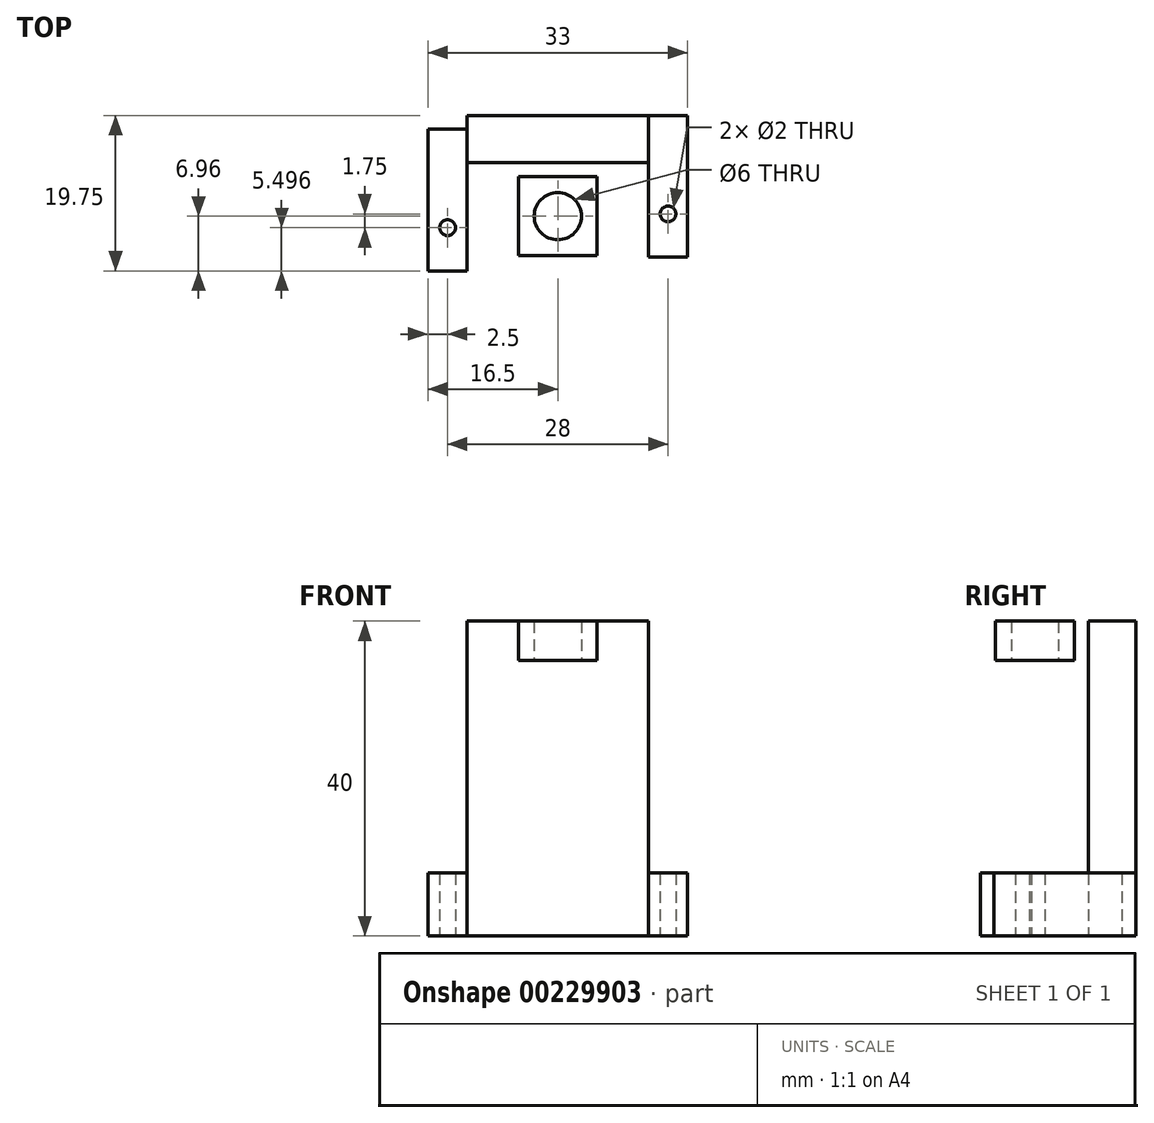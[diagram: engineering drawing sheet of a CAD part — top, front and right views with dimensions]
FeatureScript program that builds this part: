
annotation { "Feature Type Name" : "Feature", "Feature Type Description" : "" }
export const myFeature = defineFeature(function(context is Context, id is Id, definition is map)
    precondition{}
    {
        {
            var Q0;
            Q0=qCreatedBy(makeId("Top.planeOp"),FACE);
            var sketch = newSketch(context, id + "F0", { "sketchPlane" : qUnion([Q0])});
            skLineSegment(sketch, "E0.bottom", {"start": v(11.5, 7.79) * mm, "end": v(-11.5, 7.79) * mm});
            skLineSegment(sketch, "E0.top", {"start": v(11.5, 1.79) * mm, "end": v(-11.5, 1.79) * mm});
            skLineSegment(sketch, "E0.left", {"start": v(11.5, 7.79) * mm, "end": v(11.5, 1.79) * mm});
            skLineSegment(sketch, "E0.right", {"start": v(-11.5, 7.79) * mm, "end": v(-11.5, 1.79) * mm});
            skLineSegment(sketch, "E1.bottom", {"start": v(-11.5, 7.79) * mm, "end": v(-16.5, 7.79) * mm});
            skLineSegment(sketch, "E1.top", {"start": v(-11.5, -10.21) * mm, "end": v(-16.5, -10.21) * mm});
            skLineSegment(sketch, "E1.left", {"start": v(-11.5, 7.79) * mm, "end": v(-11.5, -10.21) * mm});
            skLineSegment(sketch, "E1.right", {"start": v(-16.5, 7.79) * mm, "end": v(-16.5, -10.21) * mm});
            skLineSegment(sketch, "E2.bottom", {"start": v(11.5, 7.79) * mm, "end": v(16.5, 7.79) * mm});
            skLineSegment(sketch, "E2.top", {"start": v(11.5, -10.21) * mm, "end": v(16.5, -10.21) * mm});
            skLineSegment(sketch, "E2.left", {"start": v(11.5, 7.79) * mm, "end": v(11.5, -10.21) * mm});
            skLineSegment(sketch, "E2.right", {"start": v(16.5, 7.79) * mm, "end": v(16.5, -10.21) * mm});
            skCircle(sketch, "E3", {"center": v(-14, -4.71) * mm, "radius": 1 * mm});
            skCircle(sketch, "E4", {"center": v(14, -4.71) * mm, "radius": 1 * mm});
            skSolve(sketch);
        }
        {
            var Q0;
            {var subQ3=sQuery(id+"F0.wireOp",EDGE,"E1.bottom");Q0=makeQuery(id+"F0.imprint","IMPRINT",FACE,{"disambiguationData":[TD([[makeQuery(id+"F0.imprint","IMPRINT",EDGE,{"derivedFrom":subQ3}),1.0]])]});}
            var Q1;
            {var subQ3=sQuery(id+"F0.wireOp",EDGE,"E2.bottom");Q1=makeQuery(id+"F0.imprint","IMPRINT",FACE,{"disambiguationData":[TD([[makeQuery(id+"F0.imprint","IMPRINT",EDGE,{"derivedFrom":subQ3}),-1.0]])]});}
            extrude(context, id + "F1", {"entities" : qUnion([Q0, Q1]), "depth" : 8 * mm});
        }
        {
            var Q0;
            {var subQ0=sQuery(id+"F0.wireOp",EDGE,"E0.bottom");Q0=makeQuery(id+"F0.imprint","IMPRINT",FACE,{"disambiguationData":[TD([[makeQuery(id+"F0.imprint","IMPRINT",EDGE,{"derivedFrom":subQ0}),1.0]])]});}
            extrude(context, id + "F2", {"entities" : qUnion([Q0]), "depth" : 40 * mm});
        }
        {
            var Q0;
            Q0=makeQuery(id+"F1.opExtrude","SWEPT_BODY",BODY,{"disambiguationData":[OSD([sQuery(id+"F0.wireOp",EDGE,"E1.bottom"),sQuery(id+"F0.wireOp",EDGE,"E1.top"),sQuery(id+"F0.wireOp",EDGE,"E1.left"),sQuery(id+"F0.wireOp",EDGE,"E1.right"),sQuery(id+"F0.wireOp",EDGE,"E3")])]});
            transform(context, id + "F3", {"entities" : qUnion([Q0]), "transformType" : TransformType.TRANSLATION_3D, "dx" : 0 * mm, "dy" : -1.75 * mm, "dz" : 0 * mm, "makeCopy" : false});
        }
        {
            var Q0;
            Q0=qCreatedBy(makeId("Top.planeOp"),FACE);
            var sketch = newSketch(context, id + "F4", { "sketchPlane" : qUnion([Q0])});
            skLineSegment(sketch, "E5.bottom", {"start": v(-5, 0) * mm, "end": v(5, 0) * mm});
            skLineSegment(sketch, "E5.top", {"start": v(-5, -10) * mm, "end": v(5, -10) * mm});
            skLineSegment(sketch, "E5.left", {"start": v(-5, 0) * mm, "end": v(-5, -10) * mm});
            skLineSegment(sketch, "E5.right", {"start": v(5, 0) * mm, "end": v(5, -10) * mm});
            skCircle(sketch, "E6", {"center": v(0, -5) * mm, "radius": 3 * mm});
            skSolve(sketch);
        }
        {
            var Q0;
            Q0=makeQuery(id+"F4.imprint","IMPRINT",FACE,{"disambiguationData":[TD([[makeQuery(id+"F4.imprint","IMPRINT",EDGE,{"derivedFrom":sQuery(id+"F4.wireOp",EDGE,"E5.bottom")}),-1.0]])]});
            extrude(context, id + "F5", {"entities" : qUnion([Q0]), "depth" : 40 * mm, "hasSecondDirection" : true, "secondDirectionOppositeDirection" : false, "secondDirectionDepth" : 35 * mm});
        }
    });
